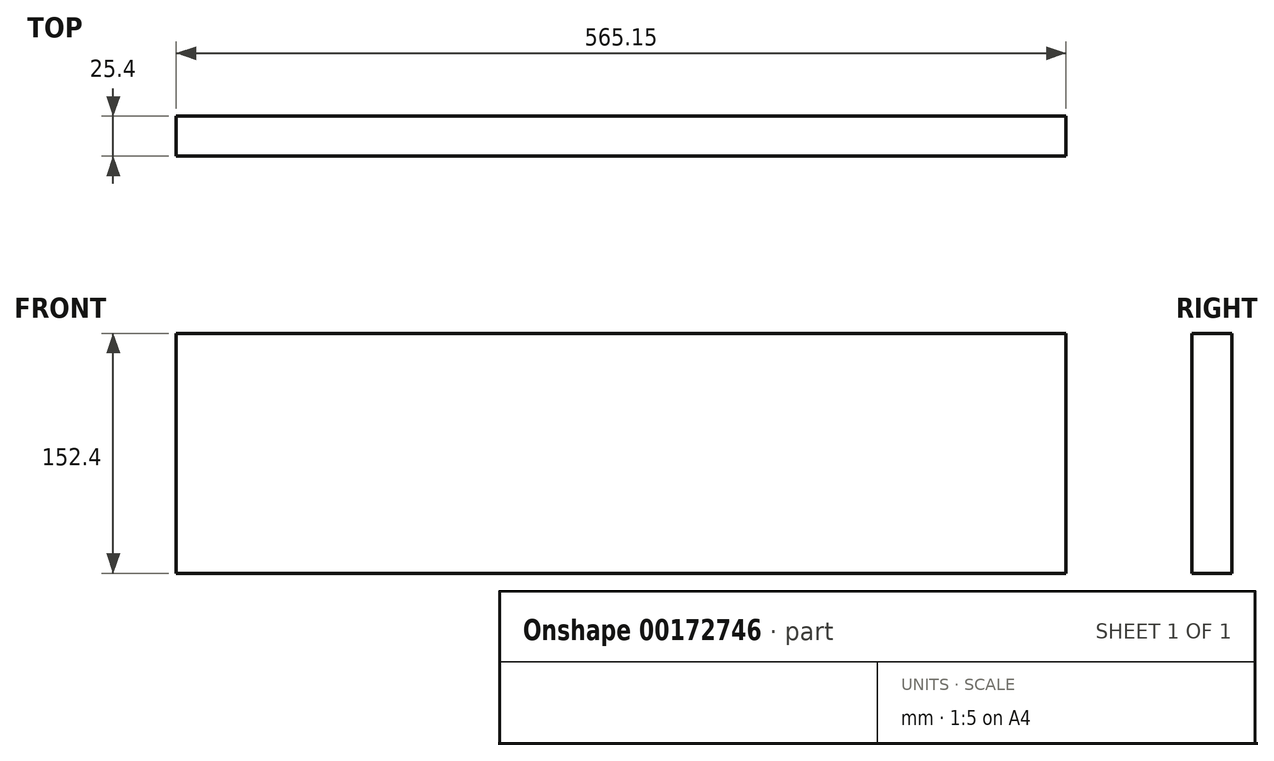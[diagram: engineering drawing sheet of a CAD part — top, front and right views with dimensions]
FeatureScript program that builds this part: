
annotation { "Feature Type Name" : "Feature", "Feature Type Description" : "" }
export const myFeature = defineFeature(function(context is Context, id is Id, definition is map)
    precondition{}
    {
        {
            var Q0;
            Q0=qCreatedBy(makeId("Front.planeOp"),FACE);
            var sketch = newSketch(context, id + "F0", { "sketchPlane" : qUnion([Q0])});
            skLineSegment(sketch, "E0.bottom", {"start": v(-283.85, 80.31) * mm, "end": v(281.3, 80.31) * mm});
            skLineSegment(sketch, "E0.top", {"start": v(-283.85, -72.09) * mm, "end": v(281.3, -72.09) * mm});
            skLineSegment(sketch, "E0.left", {"start": v(-283.85, 80.31) * mm, "end": v(-283.85, -72.09) * mm});
            skLineSegment(sketch, "E0.right", {"start": v(281.3, 80.31) * mm, "end": v(281.3, -72.09) * mm});
            skSolve(sketch);
        }
        {
            var Q0;
            Q0 = qSketchRegion(id + "F0", true);
            extrude(context, id + "F1", {"entities" : qUnion([Q0]), "depth" : 25.4 * mm});
        }
    });
